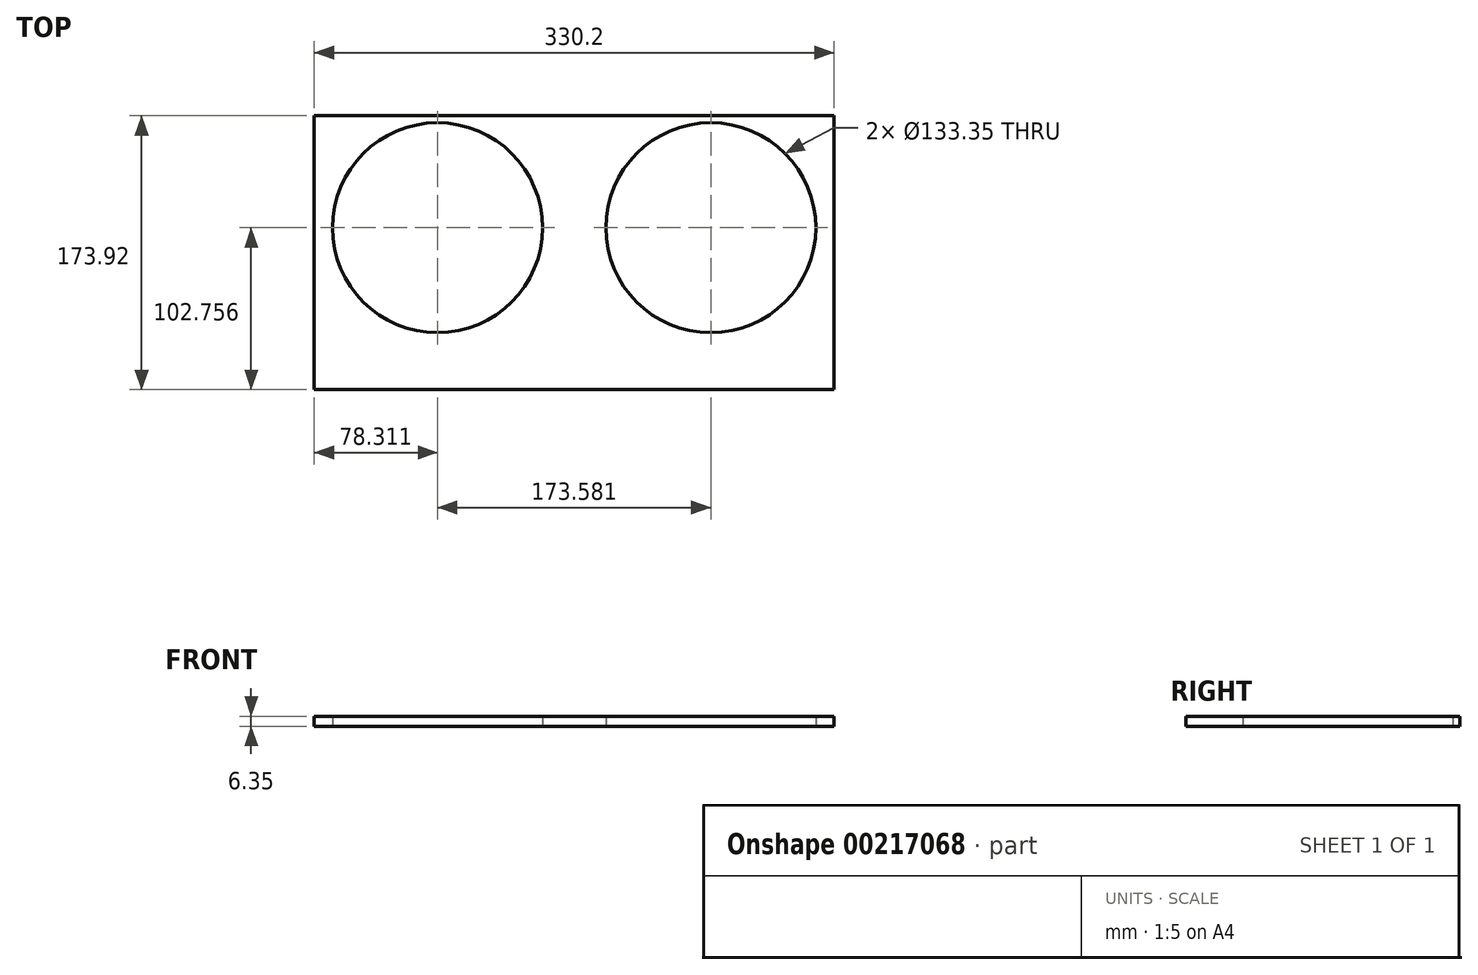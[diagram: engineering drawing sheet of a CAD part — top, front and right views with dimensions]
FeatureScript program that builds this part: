
annotation { "Feature Type Name" : "Feature", "Feature Type Description" : "" }
export const myFeature = defineFeature(function(context is Context, id is Id, definition is map)
    precondition{}
    {
        {
            var Q0;
            Q0=qCreatedBy(makeId("Top.planeOp"),FACE);
            var sketch = newSketch(context, id + "F0", { "sketchPlane" : qUnion([Q0])});
            skLineSegment(sketch, "E0.0", {"start": v(32.64, -160.95) * mm, "end": v(32.64, 12.97) * mm});
            skLineSegment(sketch, "E0.1", {"start": v(-297.56, -160.95) * mm, "end": v(32.64, -160.95) * mm});
            skLineSegment(sketch, "E0.2", {"start": v(-297.56, 12.97) * mm, "end": v(-297.56, -160.95) * mm});
            skLineSegment(sketch, "E0.3", {"start": v(32.64, 12.97) * mm, "end": v(-297.56, 12.97) * mm});
            skCircle(sketch, "E1.0", {"center": v(-219.25, -58.2) * mm, "radius": 66.67 * mm});
            skCircle(sketch, "E2.0", {"center": v(-45.67, -58.2) * mm, "radius": 66.67 * mm});
            skFitSpline(sketch, "E3.0", {"points": [v(-140.5, -141.28) * mm, v(-138.92, -141.36) * mm, v(-137.34, -141.28) * mm, v(-135.26, -140.95) * mm, v(-133.26, -140.3) * mm, v(-131.36, -139.36) * mm, v(-129.56, -138.22) * mm, v(-127.56, -136.48) * mm, v(-125.92, -134.38) * mm, v(-124.86, -132.5) * mm, v(-123.99, -130.55) * mm, v(-123.4, -128.49) * mm, v(-123.1, -126.36) * mm, v(-123.02, -124.75) * mm, v(-123.1, -123.13) * mm, v(-123.4, -121) * mm, v(-123.99, -118.94) * mm, v(-124.86, -116.98) * mm, v(-125.92, -115.11) * mm, v(-127.56, -113) * mm, v(-129.56, -111.27) * mm, v(-131.36, -110.13) * mm, v(-133.26, -109.18) * mm, v(-135.26, -108.54) * mm, v(-137.34, -108.21) * mm, v(-138.92, -108.13) * mm, v(-140.5, -108.21) * mm, v(-142.58, -108.54) * mm, v(-144.59, -109.18) * mm, v(-146.48, -110.13) * mm, v(-148.28, -111.27) * mm, v(-150.28, -113) * mm, v(-151.92, -115.11) * mm, v(-152.98, -116.98) * mm, v(-153.85, -118.94) * mm, v(-154.45, -121) * mm, v(-154.74, -123.13) * mm, v(-154.82, -124.75) * mm, v(-154.74, -126.36) * mm, v(-154.45, -128.49) * mm, v(-153.85, -130.55) * mm, v(-152.98, -132.5) * mm, v(-151.92, -134.38) * mm, v(-150.28, -136.48) * mm, v(-148.28, -138.22) * mm, v(-146.48, -139.36) * mm, v(-144.59, -140.3) * mm, v(-142.58, -140.95) * mm, v(-140.5, -141.28) * mm, v(-138.92, -141.36) * mm, v(-137.34, -141.28) * mm, v(-140.5, -141.28) * mm]});
            skSolve(sketch);
        }
        {
            var Q0;
            Q0=makeQuery(id+"F0.imprint","IMPRINT",FACE,{"disambiguationData":[TD([[makeQuery(id+"F0.imprint","IMPRINT",EDGE,{"derivedFrom":sQuery(id+"F0.wireOp",EDGE,"E0.0")}),1.0]])]});
            extrude(context, id + "F1", {"entities" : qUnion([Q0]), "depth" : 6.35 * mm});
        }
    });
